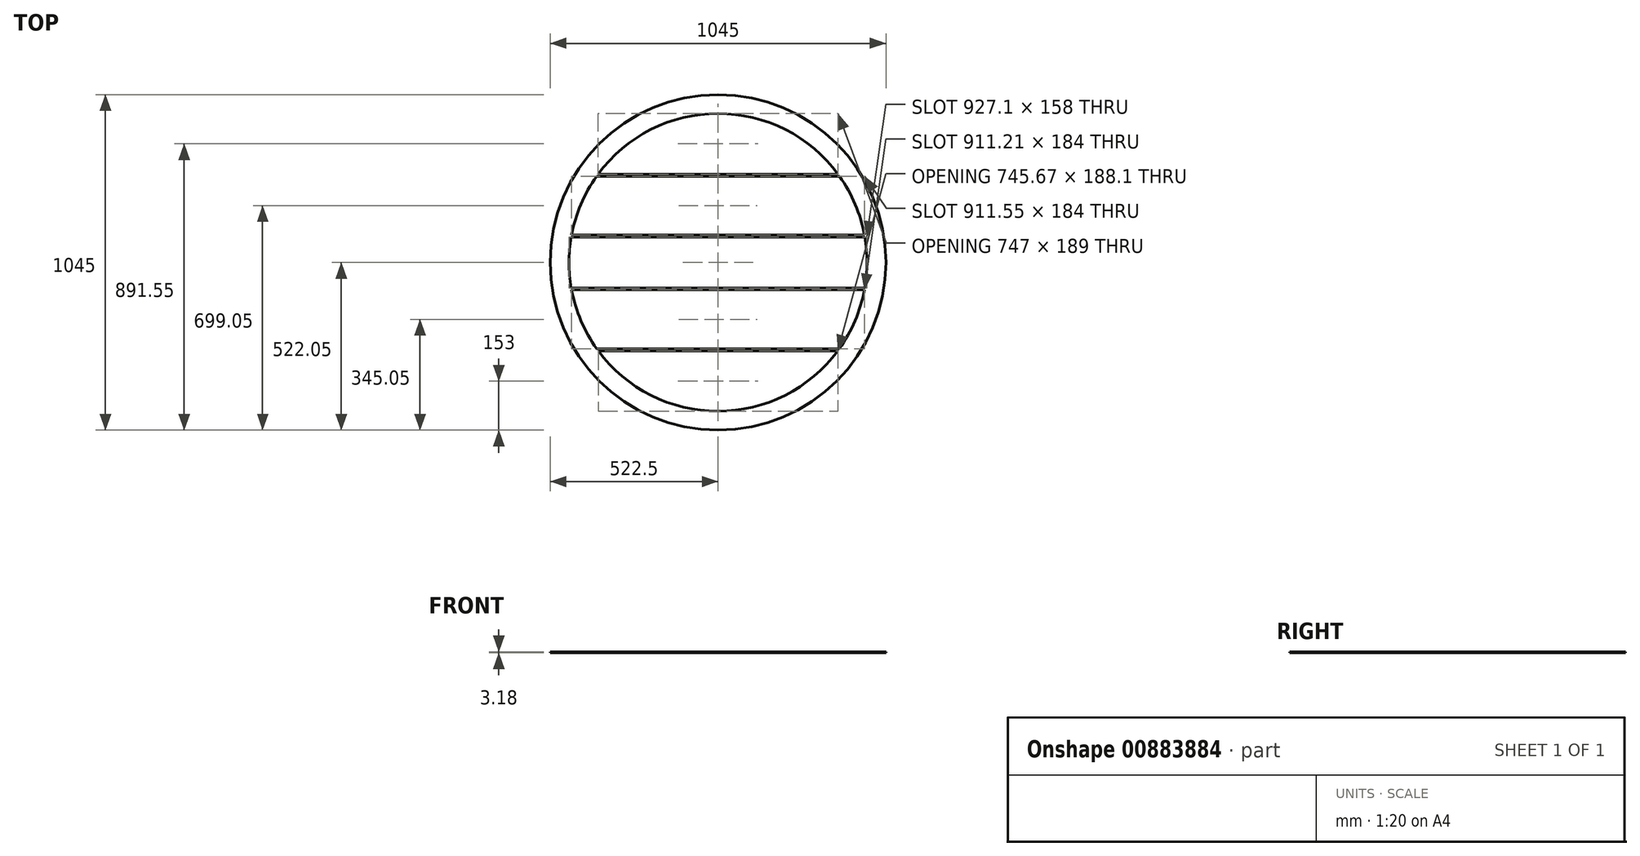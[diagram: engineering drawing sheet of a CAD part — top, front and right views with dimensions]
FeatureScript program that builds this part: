
annotation { "Feature Type Name" : "Feature", "Feature Type Description" : "" }
export const myFeature = defineFeature(function(context is Context, id is Id, definition is map)
    precondition{}
    {
        {
            var Q0;
            Q0=qCreatedBy(makeId("Top.planeOp"),FACE);
            var sketch = newSketch(context, id + "F0", { "sketchPlane" : qUnion([Q0])});
            skCircle(sketch, "E0", {"center": v(0, 0) * mm, "radius": 463.55 * mm});
            skCircle(sketch, "E1", {"center": v(0, 0) * mm, "radius": 522.5 * mm});
            skLineSegment(sketch, "E2", {"start": v(-550.36, 0) * mm, "end": v(583.91, 0) * mm, "construction": true});
            skLineSegment(sketch, "E3", {"start": v(0, 554.6) * mm, "end": v(0, -579.9) * mm, "construction": true});
            skLineSegment(sketch, "E4", {"start": v(-373.5, 274.55) * mm, "end": v(373.5, 274.55) * mm});
            skLineSegment(sketch, "E5", {"start": v(-377.84, 268.55) * mm, "end": v(377.84, 268.55) * mm});
            skLineSegment(sketch, "E6", {"start": v(-455.77, 84.55) * mm, "end": v(455.77, 84.55) * mm});
            skLineSegment(sketch, "E7", {"start": v(-456.85, 78.55) * mm, "end": v(456.85, 78.55) * mm});
            skLineSegment(sketch, "E8", {"start": v(-455.6, -85.45) * mm, "end": v(455.6, -85.45) * mm});
            skLineSegment(sketch, "E9", {"start": v(-456.7, -79.45) * mm, "end": v(456.7, -79.45) * mm});
            skLineSegment(sketch, "E10", {"start": v(-377.2, -269.45) * mm, "end": v(377.2, -269.45) * mm});
            skLineSegment(sketch, "E11", {"start": v(-372.83, -275.45) * mm, "end": v(372.83, -275.45) * mm});
            skPoint(sketch, "E12", {"position": v(0, 463.55) * mm});
            skPoint(sketch, "E13", {"position": v(373.5, 274.55) * mm});
            skSolve(sketch);
        }
        {
            var Q0;
            Q0 = qSketchRegion(id + "F0", true);
            var Q1;
            {var subQ0=sQuery(id+"F0.wireOp",EDGE,"E4");Q1=makeQuery(id+"F0.imprint","IMPRINT",FACE,{"disambiguationData":[TD([[makeQuery(id+"F0.imprint","IMPRINT",EDGE,{"derivedFrom":subQ0}),-1.0]])]});}
            var Q2;
            {var subQ0=sQuery(id+"F0.wireOp",EDGE,"E6");Q2=makeQuery(id+"F0.imprint","IMPRINT",FACE,{"disambiguationData":[TD([[makeQuery(id+"F0.imprint","IMPRINT",EDGE,{"derivedFrom":subQ0}),-1.0]])]});}
            var Q3;
            {var subQ0=sQuery(id+"F0.wireOp",EDGE,"E8");Q3=makeQuery(id+"F0.imprint","IMPRINT",FACE,{"disambiguationData":[TD([[makeQuery(id+"F0.imprint","IMPRINT",EDGE,{"derivedFrom":subQ0}),1.0]])]});}
            var Q4;
            {var subQ0=sQuery(id+"F0.wireOp",EDGE,"E10");Q4=makeQuery(id+"F0.imprint","IMPRINT",FACE,{"disambiguationData":[TD([[makeQuery(id+"F0.imprint","IMPRINT",EDGE,{"derivedFrom":subQ0}),-1.0]])]});}
            extrude(context, id + "F1", {"entities" : qUnion([Q0, Q1, Q2, Q3, Q4]), "depth" : 3.18 * mm, "offsetDistance" : 25 * mm});
        }
    });
